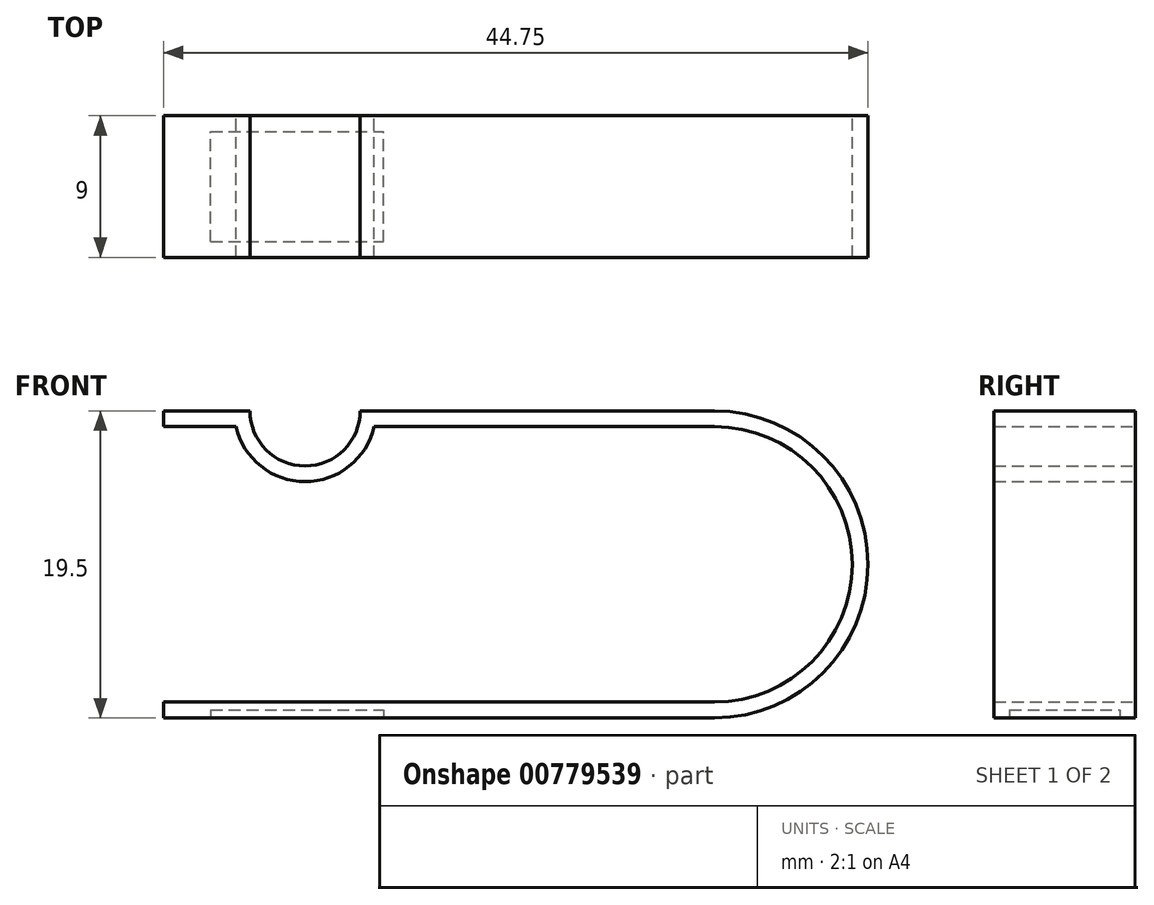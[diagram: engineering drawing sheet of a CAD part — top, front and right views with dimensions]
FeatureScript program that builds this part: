
annotation { "Feature Type Name" : "Feature", "Feature Type Description" : "" }
export const myFeature = defineFeature(function(context is Context, id is Id, definition is map)
    precondition{}
    {
        {
            var Q0;
            Q0=qCreatedBy(makeId("Front.planeOp"),FACE);
            var sketch = newSketch(context, id + "F0", { "sketchPlane" : qUnion([Q0])});
            skLineSegment(sketch, "E0", {"start": v(0, 0) * mm, "end": v(35, 0) * mm});
            skLineSegment(sketch, "E1", {"start": v(35, 19.5) * mm, "end": v(12.5, 19.5) * mm});
            skArc(sketch, "E2", {"start": v(5.5, 19.5) * mm, "mid": v(9, 16) * mm, "end": v(12.5, 19.5) * mm});
            skArc(sketch, "E3", {"start": v(35, 0) * mm, "mid": v(44.75, 9.75) * mm, "end": v(35, 19.5) * mm});
            skLineSegment(sketch, "E4.trimOffspring", {"start": v(5.5, 19.5) * mm, "end": v(0, 19.5) * mm});
            skLineSegment(sketch, "E5.0", {"start": v(4.61, 18.5) * mm, "end": v(0, 18.5) * mm});
            skLineSegment(sketch, "E5.1", {"start": v(0, 1) * mm, "end": v(35, 1) * mm});
            skArc(sketch, "E5.2", {"start": v(35, 1) * mm, "mid": v(43.75, 9.75) * mm, "end": v(35, 18.5) * mm});
            skLineSegment(sketch, "E5.3", {"start": v(35, 18.5) * mm, "end": v(13.39, 18.5) * mm});
            skArc(sketch, "E5.4", {"start": v(4.61, 18.5) * mm, "mid": v(9, 15) * mm, "end": v(13.39, 18.5) * mm});
            skLineSegment(sketch, "E6", {"start": v(0, 19.5) * mm, "end": v(0, 18.5) * mm});
            skLineSegment(sketch, "E7", {"start": v(0, 1) * mm, "end": v(0, 0) * mm});
            skSolve(sketch);
        }
        {
            var Q0;
            Q0=makeQuery(id+"F0.imprint","IMPRINT",FACE,{"disambiguationData":[TD([[makeQuery(id+"F0.imprint","IMPRINT",EDGE,{"derivedFrom":sQuery(id+"F0.wireOp",EDGE,"E0")}),1.0]])]});
            extrude(context, id + "F1", {"entities" : qUnion([Q0]), "depth" : 9 * mm, "offsetDistance" : 25 * mm});
        }
        {
            var Q0;
            Q0=makeQuery(id+"F1.opExtrude","SWEPT_FACE",FACE,{"disambiguationData":[OSD([sQuery(id+"F0.wireOp",EDGE,"E0")])]});
            var sketch = newSketch(context, id + "F2", { "sketchPlane" : qUnion([Q0])});
            skLineSegment(sketch, "E8.bottom", {"start": v(3, 8) * mm, "end": v(14, 8) * mm});
            skLineSegment(sketch, "E8.top", {"start": v(3, 1) * mm, "end": v(14, 1) * mm});
            skLineSegment(sketch, "E8.left", {"start": v(3, 8) * mm, "end": v(3, 1) * mm});
            skLineSegment(sketch, "E8.right", {"start": v(14, 8) * mm, "end": v(14, 1) * mm});
            skSolve(sketch);
        }
        {
            var Q0;
            Q0=makeQuery(id+"F2.imprint","IMPRINT",FACE,{"disambiguationData":[TD([[makeQuery(id+"F2.imprint","IMPRINT",EDGE,{"derivedFrom":sQuery(id+"F2.wireOp",EDGE,"E8.bottom")}),-1.0]])]});
            extrude(context, id + "F3", {"entities" : qUnion([Q0]), "operationType" : NewBodyOperationType.REMOVE, "oppositeDirection" : true, "depth" : 0.5 * mm, "offsetDistance" : 25 * mm});
        }
    });
